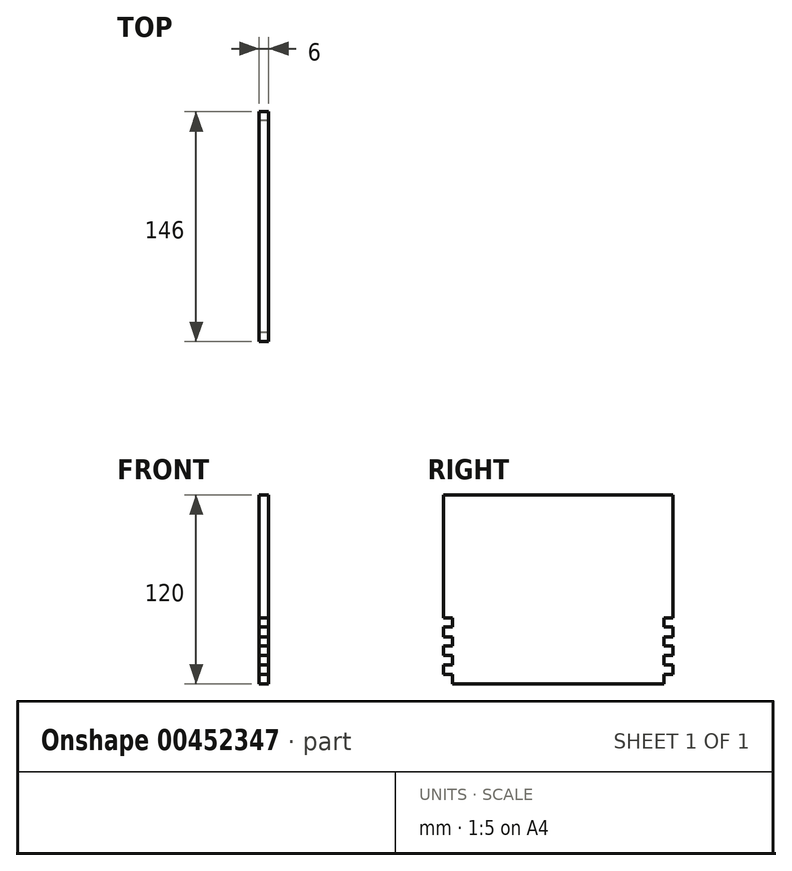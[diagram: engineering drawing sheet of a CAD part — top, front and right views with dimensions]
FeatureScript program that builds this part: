
annotation { "Feature Type Name" : "Feature", "Feature Type Description" : "" }
export const myFeature = defineFeature(function(context is Context, id is Id, definition is map)
    precondition{}
    {
        {
            var Q0;
            Q0=qCreatedBy(makeId("Right.planeOp"),FACE);
            var sketch = newSketch(context, id + "F0", { "sketchPlane" : qUnion([Q0])});
            skLineSegment(sketch, "E0", {"start": v(67.2, -60) * mm, "end": v(67.2, -54) * mm});
            skLineSegment(sketch, "E1", {"start": v(67.2, -54) * mm, "end": v(73, -54) * mm});
            skLineSegment(sketch, "E2", {"start": v(73, -54) * mm, "end": v(73, -47.8) * mm});
            skLineSegment(sketch, "E3", {"start": v(73, -47.8) * mm, "end": v(67.2, -47.8) * mm});
            skLineSegment(sketch, "E4", {"start": v(67.2, -47.8) * mm, "end": v(67.2, -42) * mm});
            skLineSegment(sketch, "E5", {"start": v(67.2, -42) * mm, "end": v(73, -42) * mm});
            skLineSegment(sketch, "E6", {"start": v(73, -42) * mm, "end": v(73, -35.8) * mm});
            skLineSegment(sketch, "E7", {"start": v(73, -35.8) * mm, "end": v(67.2, -35.8) * mm});
            skLineSegment(sketch, "E8", {"start": v(67.2, -35.8) * mm, "end": v(67.2, -30) * mm});
            skLineSegment(sketch, "E9", {"start": v(67.2, -30) * mm, "end": v(73, -30) * mm});
            skLineSegment(sketch, "E10", {"start": v(73, -30) * mm, "end": v(73, -23.8) * mm});
            skLineSegment(sketch, "E11", {"start": v(73, -23.8) * mm, "end": v(67.2, -23.8) * mm});
            skLineSegment(sketch, "E12", {"start": v(67.2, -23.8) * mm, "end": v(67.2, -18) * mm});
            skLineSegment(sketch, "E13", {"start": v(67.2, -18) * mm, "end": v(73, -18) * mm});
            skLineSegment(sketch, "E14", {"start": v(73, -18) * mm, "end": v(73, 60) * mm});
            skLineSegment(sketch, "E15.MirrorCS", {"start": v(-73, -18) * mm, "end": v(-73, 60) * mm});
            skLineSegment(sketch, "E16.MirrorCS", {"start": v(-73, -42) * mm, "end": v(-73, -35.8) * mm});
            skLineSegment(sketch, "E17.MirrorCS", {"start": v(-67.2, -60) * mm, "end": v(-67.2, -54) * mm});
            skLineSegment(sketch, "E18.MirrorCS", {"start": v(-67.2, -54) * mm, "end": v(-73, -54) * mm});
            skLineSegment(sketch, "E19.MirrorCS", {"start": v(-73, -54) * mm, "end": v(-73, -47.8) * mm});
            skLineSegment(sketch, "E20.MirrorCS", {"start": v(-73, -47.8) * mm, "end": v(-67.2, -47.8) * mm});
            skLineSegment(sketch, "E21.MirrorCS", {"start": v(-67.2, -18) * mm, "end": v(-73, -18) * mm});
            skLineSegment(sketch, "E22.MirrorCS", {"start": v(-67.2, -47.8) * mm, "end": v(-67.2, -42) * mm});
            skLineSegment(sketch, "E23.MirrorCS", {"start": v(-67.2, -23.8) * mm, "end": v(-67.2, -18) * mm});
            skLineSegment(sketch, "E24.MirrorCS", {"start": v(-73, -23.8) * mm, "end": v(-67.2, -23.8) * mm});
            skLineSegment(sketch, "E25.MirrorCS", {"start": v(-73, -30) * mm, "end": v(-73, -23.8) * mm});
            skLineSegment(sketch, "E26.MirrorCS", {"start": v(-67.2, -30) * mm, "end": v(-73, -30) * mm});
            skLineSegment(sketch, "E27.MirrorCS", {"start": v(-73, -35.8) * mm, "end": v(-67.2, -35.8) * mm});
            skLineSegment(sketch, "E28.MirrorCS", {"start": v(-67.2, -35.8) * mm, "end": v(-67.2, -30) * mm});
            skLineSegment(sketch, "E29.MirrorCS", {"start": v(-67.2, -42) * mm, "end": v(-73, -42) * mm});
            skLineSegment(sketch, "E30", {"start": v(-73, 60) * mm, "end": v(73, 60) * mm});
            skLineSegment(sketch, "E31", {"start": v(-67.2, -60) * mm, "end": v(67.2, -60) * mm});
            skLineSegment(sketch, "E32", {"start": v(-67.2, 0) * mm, "end": v(-67.2, -60) * mm, "construction": true});
            skLineSegment(sketch, "E33", {"start": v(67.2, -60) * mm, "end": v(67.2, 0) * mm, "construction": true});
            skSolve(sketch);
        }
        {
            var Q0;
            Q0 = qSketchRegion(id + "F0", true);
            extrude(context, id + "F1", {"entities" : qUnion([Q0]), "depth" : 6 * mm});
        }
    });
